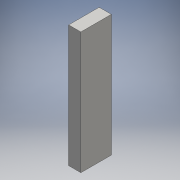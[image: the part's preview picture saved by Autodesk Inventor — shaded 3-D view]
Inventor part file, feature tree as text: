
AUTODESK INVENTOR PART (.ipt)
format: ipt  version: 2016 (Build 200138000, 138)  size: 87,040 bytes
history: native  units: mm
features: other x1, extrude x1, sketch x1
ambient origin geometry x8: Origin, YZ Plane, XZ Plane, XY Plane, X Axis, Y Axis, Z Axis, Center Point
bodies: Body1 (feature_tree)
feature tree (3):
  other  "Bryła1"
  extrude  "Wyciągnięcie proste1"  Depth=40.0mm
  sketch  "Szkic1"
